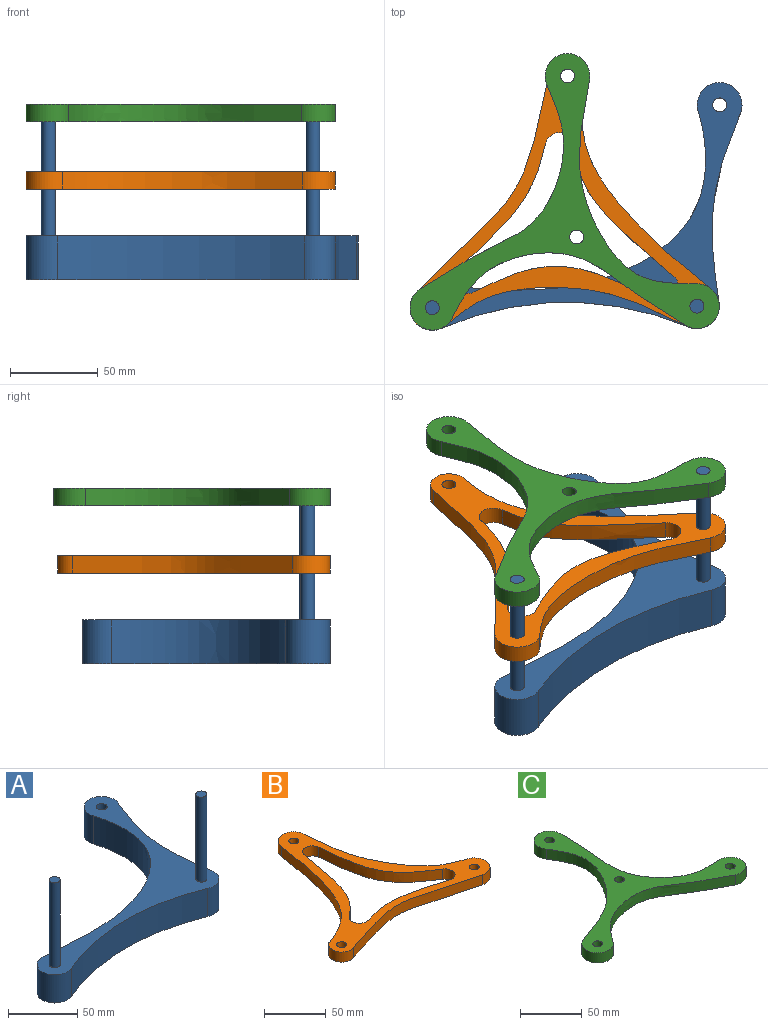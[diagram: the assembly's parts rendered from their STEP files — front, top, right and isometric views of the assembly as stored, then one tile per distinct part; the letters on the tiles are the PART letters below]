
ASSEMBLY  parts=3 mates=4
PART A: 13 faces, bbox 189.2x141.2x100 mm
  f0: extruded ~155.97x101.99mm, area 5570.9mm2, adj f1,f6,f7,f8
  f1: cylinder r=12.75mm len=25.5mm, axis (0,0,-1), area 1128.5mm2, adj f0,f2,f7,f8
  f2: cylinder r=178.17mm len=140.61mm, axis (0,0,-1), area 3613.6mm2, adj f1,f3,f7,f8
  f3: cylinder r=12.75mm len=25mm, axis (0,0,-1), area 676.5mm2, adj f2,f4,f7,f8
  f4: extruded ~107.7x25mm, area 2759mm2, adj f3,f6,f7,f8
  f5: cylinder r=3.97mm len=25mm, axis (0,0,-1), area 623.4mm2, adj f7,f8
  f6: cylinder r=12.75mm len=25.5mm, axis (0,0,-1), area 1226.3mm2, adj f0,f4,f7,f8
  f7: plane 189.22x141.19mm, normal (0,0,1), area 4953.9mm2, adj f0,f1,f2,f3,f4,f5,f6,f9
  f8: plane 189.22x141.19mm, normal (0,0,-1), area 5052.9mm2, adj f0,f1,f2,f3,f4,f5,f6
  f9: cylinder r=3.97mm len=75mm, axis (0,0,-1), area 1870.2mm2, adj f7,f10
  f10: plane 7.94x7.94mm, normal (0,0,1), area 49.5mm2, adj f9
  f11: cylinder r=3.97mm len=75mm, axis (0,0,-1), area 1870.2mm2, adj f7,f12
  f12: plane 7.94x7.94mm, normal (0,0,1), area 49.5mm2, adj f11
PART B: 17 faces, bbox 176.1x154.8x10 mm
  f0: cylinder r=8.27mm len=14.75mm, axis (0,0,-1), area 229.3mm2, adj f1,f14,f15,f16
  f1: extruded ~87.08x35.65mm, area 969.7mm2, adj f0,f2,f15,f16
  f2: cylinder r=8.14mm len=16.09mm, axis (0,0,-1), area 232.2mm2, adj f1,f3,f15,f16
  f3: extruded ~92.6x49.25mm, area 1111.4mm2, adj f2,f4,f15,f16
  f4: cylinder r=8.18mm len=15.08mm, axis (0,0,-1), area 236.6mm2, adj f3,f14,f15,f16
  f5: extruded ~118.1x69.03mm, area 1464.8mm2, adj f6,f13,f15,f16
  f6: cylinder r=12.75mm len=25.38mm, axis (0,0,-1), area 377.1mm2, adj f5,f7,f15,f16
  f7: extruded ~121.79x66.05mm, area 1474.1mm2, adj f6,f8,f15,f16
  f8: cylinder r=10.5mm len=20.44mm, axis (0,0,-1), area 329.7mm2, adj f7,f9,f15,f16
  f9: extruded ~146.51x18.56mm, area 1512.6mm2, adj f8,f13,f15,f16
  f10: cylinder r=3.97mm len=10mm, axis (0,0,-1), area 249.4mm2, adj f15,f16
  f11: cylinder r=3.97mm len=10mm, axis (0,0,-1), area 249.4mm2, adj f15,f16
  f12: cylinder r=3.97mm len=10mm, axis (0,0,-1), area 249.4mm2, adj f15,f16
  f13: cylinder r=12.75mm len=24.78mm, axis (0,0,-1), area 388.1mm2, adj f5,f9,f15,f16
  f14: extruded ~86.4x12.11mm, area 885.5mm2, adj f0,f4,f15,f16
  f15: plane 176.12x154.79mm, normal (0,0,1), area 4842.5mm2, adj f0,f1,f2,f3,f4,f5,f6,f7
  f16: plane 176.12x154.79mm, normal (0,0,-1), area 4842.5mm2, adj f0,f1,f2,f3,f4,f5,f6,f7
PART C: 12 faces, bbox 178.4x155.7x10 mm
  f0: extruded ~111.55x81.39mm, area 1563.2mm2, adj f1,f8,f10,f11
  f1: cylinder r=12.75mm len=24.75mm, axis (0,0,-1), area 479.4mm2, adj f0,f2,f10,f11
  f2: extruded ~136.73x37.66mm, area 1589.1mm2, adj f1,f3,f10,f11
  f3: cylinder r=12.75mm len=25.5mm, axis (0,0,-1), area 466.5mm2, adj f2,f4,f10,f11
  f4: extruded ~116.87x67.46mm, area 1603.3mm2, adj f3,f8,f10,f11
  f5: cylinder r=3.97mm len=10mm, axis (0,0,-1), area 249.4mm2, adj f10,f11
  f6: cylinder r=3.97mm len=10mm, axis (0,0,-1), area 249.4mm2, adj f10,f11
  f7: cylinder r=3.97mm len=10mm, axis (0,0,-1), area 249.4mm2, adj f10,f11
  f8: cylinder r=12.75mm len=25.5mm, axis (0,0,-1), area 472.3mm2, adj f0,f4,f10,f11
  f9: cylinder r=3.97mm len=10mm, axis (0,0,-1), area 249.4mm2, adj f10,f11
  f10: plane 178.37x155.73mm, normal (0,0,1), area 4619.4mm2, adj f0,f1,f2,f3,f4,f5,f6,f7
  f11: plane 178.37x155.73mm, normal (0,0,-1), area 4619.4mm2, adj f0,f1,f2,f3,f4,f5,f6,f7
PLACE A t=(-404.26,271.53,-3.32)mm fixed
PLACE B rot(axis=(0,0,-1),120.6deg) t=(39.45,193.34,48.33)mm
PLACE C rot(axis=(0,0,-1),120.6deg) t=(192.94,134.91,86.68)mm
MATE revolute C.f3 <-> A.f1  axis (0,0,-1) through (-153.62,-2.98,96.68)mm
MATE revolute A.f3 <-> C.f5  axis (0,0,-1) through (-2.87,-2.06,96.68)mm
MATE cylindrical B.f11 <-> A.f1  axis (0,0,-1) through (-153.62,-2.98,48.33)mm
MATE cylindrical A.f3 <-> B.f6  axis (0,0,-1) through (-2.87,-2.06,59.18)mm
